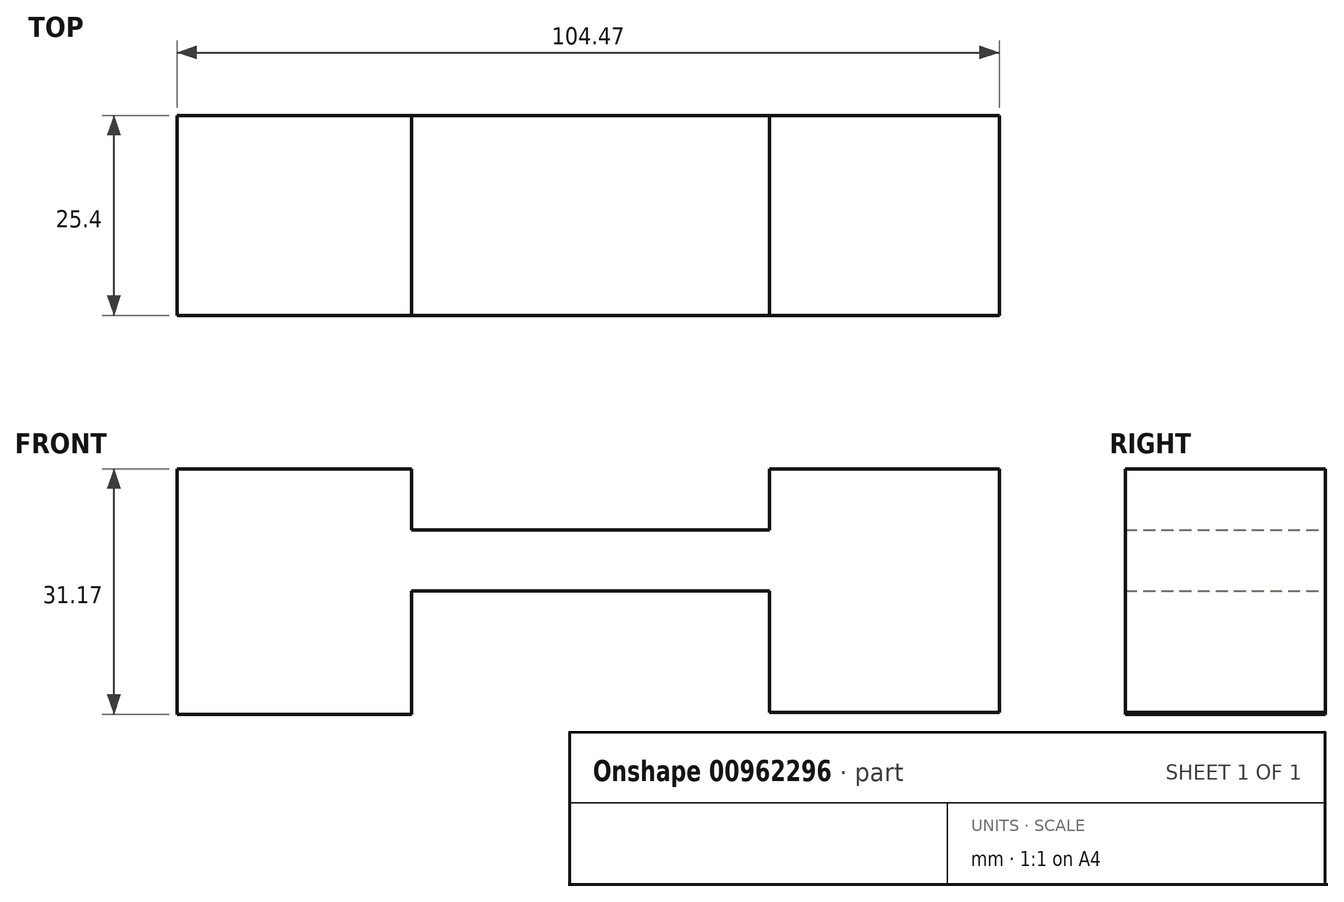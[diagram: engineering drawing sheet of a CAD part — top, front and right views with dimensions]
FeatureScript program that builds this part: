
annotation { "Feature Type Name" : "Feature", "Feature Type Description" : "" }
export const myFeature = defineFeature(function(context is Context, id is Id, definition is map)
    precondition{}
    {
        {
            var Q0;
            Q0=qCreatedBy(makeId("Front.planeOp"),FACE);
            var sketch = newSketch(context, id + "F0", { "sketchPlane" : qUnion([Q0])});
            skLineSegment(sketch, "E0.bottom", {"start": v(-51.98, 0) * mm, "end": v(-22.16, 0) * mm});
            skLineSegment(sketch, "E0.top", {"start": v(-51.98, -31.17) * mm, "end": v(-22.16, -31.17) * mm});
            skLineSegment(sketch, "E0.left", {"start": v(-51.98, 0) * mm, "end": v(-51.98, -31.17) * mm});
            skLineSegment(sketch, "E0.right", {"start": v(-22.16, 0) * mm, "end": v(-22.16, -31.17) * mm});
            skLineSegment(sketch, "E1.bottom", {"start": v(52.49, 0) * mm, "end": v(23.27, 0) * mm});
            skLineSegment(sketch, "E1.top", {"start": v(52.49, -30.97) * mm, "end": v(23.27, -30.97) * mm});
            skLineSegment(sketch, "E1.left", {"start": v(52.49, 0) * mm, "end": v(52.49, -30.97) * mm});
            skLineSegment(sketch, "E1.right", {"start": v(23.27, 0) * mm, "end": v(23.27, -30.97) * mm});
            skLineSegment(sketch, "E2.bottom", {"start": v(23.27, -15.49) * mm, "end": v(-22.16, -15.49) * mm});
            skLineSegment(sketch, "E2.top", {"start": v(23.27, -7.76) * mm, "end": v(-22.16, -7.76) * mm});
            skLineSegment(sketch, "E2.left", {"start": v(23.27, -15.49) * mm, "end": v(23.27, -7.76) * mm});
            skLineSegment(sketch, "E2.right", {"start": v(-22.16, -15.49) * mm, "end": v(-22.16, -7.76) * mm});
            skSolve(sketch);
        }
        {
            var Q0;
            Q0 = qSketchRegion(id + "F0", true);
            extrude(context, id + "F1", {"entities" : qUnion([Q0]), "depth" : 25.4 * mm, "offsetDistance" : 25.4 * mm});
        }
    });
